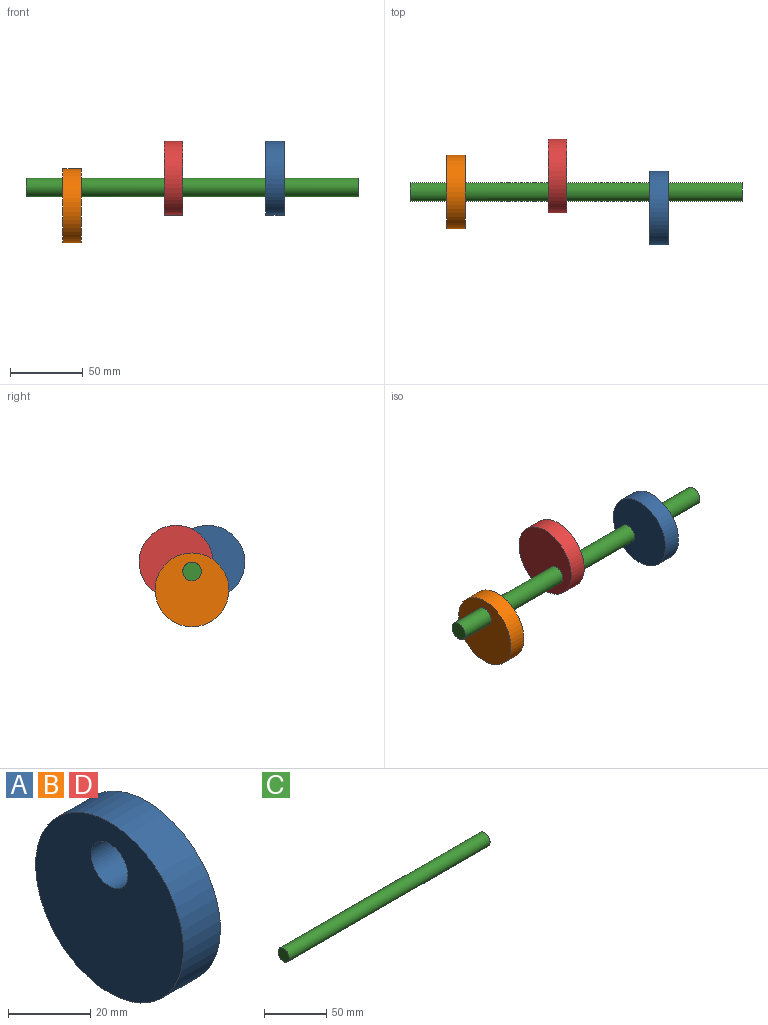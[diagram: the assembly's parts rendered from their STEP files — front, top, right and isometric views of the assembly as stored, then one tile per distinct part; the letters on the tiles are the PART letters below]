
ASSEMBLY  parts=4 mates=3
PART A: 4 faces, bbox 12.7x50.8x50.8 mm
  f0: plane 50.8x50.8mm, normal (1,0,0), area 1900.2mm2, adj f2,f3
  f1: plane 50.8x50.8mm, normal (-1,0,0), area 1900.2mm2, adj f2,f3
  f2: cylinder r=25.4mm len=50.8mm, axis (-1,0,0), area 2026.8mm2, adj f0,f1
  f3: cylinder r=6.35mm len=12.7mm, axis (-1,0,0), area 506.7mm2, adj f0,f1
PART B: same geometry as A
PART C: 3 faces, bbox 228.6x12.7x12.7 mm
  f0: plane 12.7x12.7mm, normal (-1,0,0), area 126.7mm2, adj f2
  f1: plane 12.7x12.7mm, normal (1,0,0), area 126.7mm2, adj f2
  f2: cylinder r=6.35mm len=228.6mm, axis (-1,0,0), area 9120.7mm2, adj f0,f1
PART D: same geometry as A
PLACE A rot(axis=(-1,0,0),120deg) t=(49.59,-44.2,55.33)mm
PLACE B t=(-90.11,-0.21,-20.87)mm
PLACE C t=(-90.11,-0.21,-20.87)mm
PLACE D rot(axis=(1,0,0),120deg) t=(-20.26,43.79,55.33)mm
MATE fastened C.f2 <-> A.f3  axis (1,0,0) through (-20.26,-0.21,29.93)mm
MATE fastened D.f3 <-> C.f2  axis (-1,0,0) through (-90.11,-0.21,29.93)mm
MATE fastened C.f2 <-> B.f3  axis (1,0,0) through (-159.96,-0.21,29.93)mm
